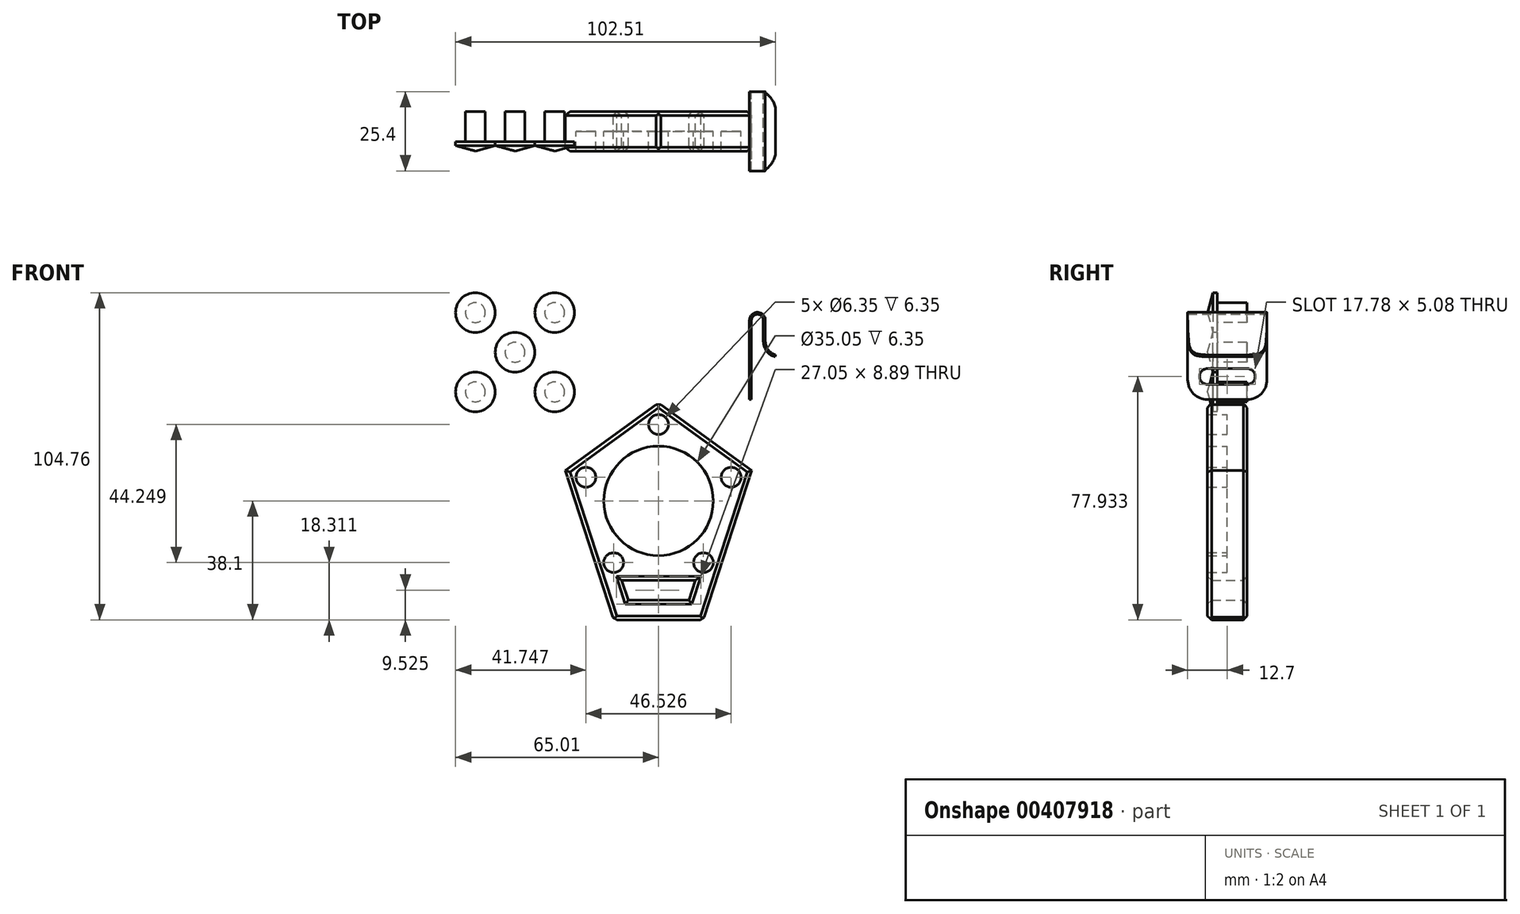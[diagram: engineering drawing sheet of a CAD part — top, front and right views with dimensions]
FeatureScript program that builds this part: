
annotation { "Feature Type Name" : "Feature", "Feature Type Description" : "" }
export const myFeature = defineFeature(function(context is Context, id is Id, definition is map)
    precondition{}
    {
        {
            var Q0;
            Q0=qCreatedBy(makeId("Front.planeOp"),FACE);
            var sketch = newSketch(context, id + "F0", { "sketchPlane" : qUnion([Q0])});
            skLineSegment(sketch, "E0.0", {"start": v(0, 31.4) * mm, "end": v(29.86, 9.7) * mm});
            skLineSegment(sketch, "E0.1", {"start": v(29.86, 9.7) * mm, "end": v(18.45, -25.4) * mm});
            skLineSegment(sketch, "E0.3", {"start": v(-18.45, -25.4) * mm, "end": v(-29.86, 9.7) * mm});
            skLineSegment(sketch, "E0.4", {"start": v(-29.86, 9.7) * mm, "end": v(0, 31.4) * mm});
            skLineSegment(sketch, "E1", {"start": v(-14.33, -38.1) * mm, "end": v(14.33, -38.1) * mm});
            skLineSegment(sketch, "E2", {"start": v(-9.71, -31.75) * mm, "end": v(9.71, -31.75) * mm});
            skLineSegment(sketch, "E3", {"start": v(11.78, -25.4) * mm, "end": v(-11.78, -25.4) * mm});
            skLineSegment(sketch, "E4", {"start": v(-18.45, -25.4) * mm, "end": v(-14.33, -38.1) * mm});
            skLineSegment(sketch, "E5", {"start": v(18.45, -25.4) * mm, "end": v(14.33, -38.1) * mm});
            skLineSegment(sketch, "E6", {"start": v(-11.78, -25.4) * mm, "end": v(-9.71, -31.75) * mm});
            skLineSegment(sketch, "E7", {"start": v(11.78, -25.4) * mm, "end": v(9.71, -31.75) * mm});
            skCircle(sketch, "E8", {"center": v(0, 0) * mm, "radius": 17.53 * mm});
            skLineSegment(sketch, "E9", {"start": v(-29.86, 9.7) * mm, "end": v(0, 0) * mm, "construction": true});
            skLineSegment(sketch, "E10", {"start": v(0, 31.4) * mm, "end": v(0, 0) * mm, "construction": true});
            skLineSegment(sketch, "E11", {"start": v(0, 0) * mm, "end": v(29.86, 9.7) * mm, "construction": true});
            skLineSegment(sketch, "E12", {"start": v(0, 0) * mm, "end": v(-18.45, -25.4) * mm, "construction": true});
            skLineSegment(sketch, "E13", {"start": v(0, 0) * mm, "end": v(18.45, -25.4) * mm, "construction": true});
            skCircle(sketch, "E14", {"center": v(-23.26, 7.56) * mm, "radius": 3.18 * mm});
            skCircle(sketch, "E15", {"center": v(0, 24.46) * mm, "radius": 3.18 * mm});
            skCircle(sketch, "E16", {"center": v(23.26, 7.56) * mm, "radius": 3.18 * mm});
            skCircle(sketch, "E17", {"center": v(14.38, -19.79) * mm, "radius": 3.18 * mm});
            skCircle(sketch, "E18", {"center": v(-14.38, -19.79) * mm, "radius": 3.18 * mm});
            skSolve(sketch);
        }
        {
            var Q0;
            Q0=makeQuery(id+"F0.imprint","IMPRINT",FACE,{"disambiguationData":[TD([[makeQuery(id+"F0.imprint","IMPRINT",EDGE,{"derivedFrom":sQuery(id+"F0.wireOp",EDGE,"E0.0")}),-1.0]])]});
            extrude(context, id + "F1", {"entities" : qUnion([Q0]), "endBound" : BoundingType.SYMMETRIC, "depth" : 12.7 * mm});
        }
        {
            var Q0;
            Q0=makeQuery(id+"F0.imprint","IMPRINT",FACE,{"disambiguationData":[TD([[makeQuery(id+"F0.imprint","IMPRINT",EDGE,{"derivedFrom":sQuery(id+"F0.wireOp",EDGE,"E8")}),1.0]])]});
            extrude(context, id + "F2", {"entities" : qUnion([Q0]), "operationType" : NewBodyOperationType.ADD, "oppositeDirection" : true, "depth" : 6.35 * mm});
        }
        {
            var Q0;
            Q0=makeQuery(id+"F0.imprint","IMPRINT",FACE,{"disambiguationData":[TD([[makeQuery(id+"F0.imprint","IMPRINT",EDGE,{"derivedFrom":sQuery(id+"F0.wireOp",EDGE,"E17")}),1.0]])]});
            var Q1;
            Q1=makeQuery(id+"F0.imprint","IMPRINT",FACE,{"disambiguationData":[TD([[makeQuery(id+"F0.imprint","IMPRINT",EDGE,{"derivedFrom":sQuery(id+"F0.wireOp",EDGE,"E16")}),1.0]])]});
            var Q2;
            Q2=makeQuery(id+"F0.imprint","IMPRINT",FACE,{"disambiguationData":[TD([[makeQuery(id+"F0.imprint","IMPRINT",EDGE,{"derivedFrom":sQuery(id+"F0.wireOp",EDGE,"E15")}),1.0]])]});
            var Q3;
            Q3=makeQuery(id+"F0.imprint","IMPRINT",FACE,{"disambiguationData":[TD([[makeQuery(id+"F0.imprint","IMPRINT",EDGE,{"derivedFrom":sQuery(id+"F0.wireOp",EDGE,"E14")}),1.0]])]});
            var Q4;
            Q4=makeQuery(id+"F0.imprint","IMPRINT",FACE,{"disambiguationData":[TD([[makeQuery(id+"F0.imprint","IMPRINT",EDGE,{"derivedFrom":sQuery(id+"F0.wireOp",EDGE,"E18")}),1.0]])]});
            extrude(context, id + "F3", {"entities" : qUnion([Q0, Q1, Q2, Q3, Q4]), "operationType" : NewBodyOperationType.ADD, "oppositeDirection" : true, "depth" : 6.35 * mm});
        }
        {
            var Q0;
            Q0=makeQuery(id+"F1.opExtrude","CAP_EDGE",EDGE,{"disambiguationData":[OSD([sQuery(id+"F0.wireOp",EDGE,"E2")])],"isStart":false});
            var Q1;
            Q1=makeQuery(id+"F1.opExtrude","CAP_EDGE",EDGE,{"disambiguationData":[OSD([sQuery(id+"F0.wireOp",EDGE,"E6")])],"isStart":false});
            var Q2;
            Q2=makeQuery(id+"F1.opExtrude","CAP_EDGE",EDGE,{"disambiguationData":[OSD([sQuery(id+"F0.wireOp",EDGE,"E3")])],"isStart":false});
            var Q3;
            Q3=makeQuery(id+"F1.opExtrude","CAP_EDGE",EDGE,{"disambiguationData":[OSD([sQuery(id+"F0.wireOp",EDGE,"E7")])],"isStart":false});
            var Q4;
            Q4=makeQuery(id+"F1.opExtrude","CAP_EDGE",EDGE,{"disambiguationData":[OSD([sQuery(id+"F0.wireOp",EDGE,"E2")])],"isStart":true});
            var Q5;
            Q5=makeQuery(id+"F1.opExtrude","CAP_EDGE",EDGE,{"disambiguationData":[OSD([sQuery(id+"F0.wireOp",EDGE,"E3")])],"isStart":true});
            var Q6;
            Q6=makeQuery(id+"F1.opExtrude","CAP_EDGE",EDGE,{"disambiguationData":[OSD([sQuery(id+"F0.wireOp",EDGE,"E6")])],"isStart":true});
            var Q7;
            Q7=makeQuery(id+"F1.opExtrude","CAP_EDGE",EDGE,{"disambiguationData":[OSD([sQuery(id+"F0.wireOp",EDGE,"E7")])],"isStart":true});
            var Q8;
            Q8=makeQuery(id+"F1.opExtrude","CAP_EDGE",EDGE,{"disambiguationData":[OSD([sQuery(id+"F0.wireOp",EDGE,"E1")])],"isStart":false});
            var Q9;
            Q9=makeQuery(id+"F1.opExtrude","CAP_EDGE",EDGE,{"disambiguationData":[OSD([sQuery(id+"F0.wireOp",EDGE,"E0.3"),sQuery(id+"F0.wireOp",EDGE,"E4")])],"isStart":false});
            var Q10;
            Q10=makeQuery(id+"F1.opExtrude","CAP_EDGE",EDGE,{"disambiguationData":[OSD([sQuery(id+"F0.wireOp",EDGE,"E0.0")])],"isStart":false});
            var Q11;
            Q11=makeQuery(id+"F1.opExtrude","CAP_EDGE",EDGE,{"disambiguationData":[OSD([sQuery(id+"F0.wireOp",EDGE,"E0.4")])],"isStart":false});
            var Q12;
            Q12=makeQuery(id+"F1.opExtrude","CAP_EDGE",EDGE,{"disambiguationData":[OSD([sQuery(id+"F0.wireOp",EDGE,"E0.4")])],"isStart":true});
            var Q13;
            Q13=makeQuery(id+"F1.opExtrude","CAP_EDGE",EDGE,{"disambiguationData":[OSD([sQuery(id+"F0.wireOp",EDGE,"E0.3"),sQuery(id+"F0.wireOp",EDGE,"E4")])],"isStart":true});
            var Q14;
            Q14=makeQuery(id+"F1.opExtrude","CAP_EDGE",EDGE,{"disambiguationData":[OSD([sQuery(id+"F0.wireOp",EDGE,"E0.1"),sQuery(id+"F0.wireOp",EDGE,"E5")])],"isStart":true});
            var Q15;
            Q15=makeQuery(id+"F1.opExtrude","CAP_EDGE",EDGE,{"disambiguationData":[OSD([sQuery(id+"F0.wireOp",EDGE,"E0.0")])],"isStart":true});
            var Q16;
            Q16=makeQuery(id+"F1.opExtrude","CAP_EDGE",EDGE,{"disambiguationData":[OSD([sQuery(id+"F0.wireOp",EDGE,"E1")])],"isStart":true});
            var Q17;
            Q17=makeQuery(id+"F1.opExtrude","CAP_EDGE",EDGE,{"disambiguationData":[OSD([sQuery(id+"F0.wireOp",EDGE,"E0.1"),sQuery(id+"F0.wireOp",EDGE,"E5")])],"isStart":false});
            chamfer(context, id + "F4", {"entities" : qUnion([Q0, Q1, Q2, Q3, Q4, Q5, Q6, Q7, Q8, Q9, Q10, Q11, Q12, Q13, Q14, Q15, Q16, Q17]), "width" : 1.27 * mm, "tangentPropagation" : true});
        }
        {
            var Q0;
            Q0=makeQuery(id+"F1.opExtrude","SWEPT_EDGE",EDGE,{"disambiguationData":[OSD([sQuery(id+"F0.wireOp",EDGE,"E0.0"),sQuery(id+"F0.wireOp",EDGE,"E0.4")])]});
            var Q1;
            Q1=makeQuery(id+"F1.opExtrude","SWEPT_EDGE",EDGE,{"disambiguationData":[OSD([sQuery(id+"F0.wireOp",EDGE,"E1"),sQuery(id+"F0.wireOp",EDGE,"E5")])]});
            var Q2;
            Q2=makeQuery(id+"F1.opExtrude","SWEPT_EDGE",EDGE,{"disambiguationData":[OSD([sQuery(id+"F0.wireOp",EDGE,"E1"),sQuery(id+"F0.wireOp",EDGE,"E4")])]});
            chamfer(context, id + "F5", {"entities" : qUnion([Q0, Q1, Q2]), "width" : 1.27 * mm, "tangentPropagation" : true});
        }
        {
            var Q0;
            Q0=qCreatedBy(makeId("Front.planeOp"),FACE);
            var sketch = newSketch(context, id + "F6", { "sketchPlane" : qUnion([Q0])});
            skLineSegment(sketch, "E19", {"start": v(-61.83, 38.2) * mm, "end": v(-61.83, 28.56) * mm});
            skLineSegment(sketch, "E20", {"start": v(-58.66, 28.56) * mm, "end": v(-61.83, 28.56) * mm});
            skLineSegment(sketch, "E21", {"start": v(-61.83, 38.2) * mm, "end": v(-65, 38.2) * mm});
            skLineSegment(sketch, "E22", {"start": v(-58.66, 41.26) * mm, "end": v(-58.66, 28.56) * mm});
            skLineSegment(sketch, "E23", {"start": v(-65, 38.2) * mm, "end": v(-65, 39.48) * mm});
            skLineSegment(sketch, "E24", {"start": v(-65, 39.48) * mm, "end": v(-58.66, 41.26) * mm});
            skLineSegment(sketch, "E25", {"start": v(-75.18, 34.9) * mm, "end": v(-45.79, 34.9) * mm, "construction": true});
            skSolve(sketch);
        }
        {
            var Q0;
            Q0 = qSketchRegion(id + "F6", true);
            var Q1;
            Q1=sQuery(id+"F6.wireOp",EDGE,"E22");
            revolve(context, id + "F7", {"entities" : qUnion([Q0]), "axis" : qUnion([Q1]), "revolveType" : RevolveType.FULL});
        }
        {
            var Q0;
            Q0=makeQuery(id+"F7.opRevolve","SWEPT_BODY",BODY,{"disambiguationData":[OSD([sQuery(id+"F6.wireOp",EDGE,"E19"),sQuery(id+"F6.wireOp",EDGE,"E20"),sQuery(id+"F6.wireOp",EDGE,"E21"),sQuery(id+"F6.wireOp",EDGE,"E22"),sQuery(id+"F6.wireOp",EDGE,"E23"),sQuery(id+"F6.wireOp",EDGE,"E24")])]});
            var Q1;
            Q1=sQuery(id+"F6.wireOp",EDGE,"E25");
            transform(context, id + "F8", {"entities" : qUnion([Q0]), "transformType" : TransformType.ROTATION, "transformAxis" : qUnion([Q1]), "angle" : 90 * degree, "makeCopy" : false});
        }
        {
            var Q0;
            Q0=makeQuery(id+"F7.opRevolve","SWEPT_BODY",BODY,{"disambiguationData":[OSD([sQuery(id+"F6.wireOp",EDGE,"E19"),sQuery(id+"F6.wireOp",EDGE,"E20"),sQuery(id+"F6.wireOp",EDGE,"E21"),sQuery(id+"F6.wireOp",EDGE,"E22"),sQuery(id+"F6.wireOp",EDGE,"E23"),sQuery(id+"F6.wireOp",EDGE,"E24")])]});
            transform(context, id + "F9", {"entities" : qUnion([Q0]), "transformType" : TransformType.TRANSLATION_3D, "dx" : 0 * mm, "dy" : 0 * mm, "dz" : 25.4 * mm, "makeCopy" : true});
        }
        {
            var Q0;
            Q0=makeQuery(id+"F9.opPattern","COPY",BODY,{"derivedFrom":makeQuery(id+"F7.opRevolve","SWEPT_BODY",BODY,{"disambiguationData":[OSD([sQuery(id+"F6.wireOp",EDGE,"E19"),sQuery(id+"F6.wireOp",EDGE,"E20"),sQuery(id+"F6.wireOp",EDGE,"E21"),sQuery(id+"F6.wireOp",EDGE,"E22"),sQuery(id+"F6.wireOp",EDGE,"E23"),sQuery(id+"F6.wireOp",EDGE,"E24")])]}),"instanceName":"1"});
            transform(context, id + "F10", {"entities" : qUnion([Q0]), "transformType" : TransformType.TRANSLATION_3D, "dx" : 25.4 * mm, "dy" : 0 * mm, "dz" : 0 * mm, "makeCopy" : true});
        }
        {
            var Q0;
            Q0=makeQuery(id+"F7.opRevolve","SWEPT_BODY",BODY,{"disambiguationData":[OSD([sQuery(id+"F6.wireOp",EDGE,"E19"),sQuery(id+"F6.wireOp",EDGE,"E20"),sQuery(id+"F6.wireOp",EDGE,"E21"),sQuery(id+"F6.wireOp",EDGE,"E22"),sQuery(id+"F6.wireOp",EDGE,"E23"),sQuery(id+"F6.wireOp",EDGE,"E24")])]});
            transform(context, id + "F11", {"entities" : qUnion([Q0]), "transformType" : TransformType.TRANSLATION_3D, "dx" : 25.4 * mm, "dy" : 0 * mm, "dz" : 0 * mm, "makeCopy" : true});
        }
        {
            var Q0;
            Q0=makeQuery(id+"F7.opRevolve","SWEPT_BODY",BODY,{"disambiguationData":[OSD([sQuery(id+"F6.wireOp",EDGE,"E19"),sQuery(id+"F6.wireOp",EDGE,"E20"),sQuery(id+"F6.wireOp",EDGE,"E21"),sQuery(id+"F6.wireOp",EDGE,"E22"),sQuery(id+"F6.wireOp",EDGE,"E23"),sQuery(id+"F6.wireOp",EDGE,"E24")])]});
            transform(context, id + "F12", {"entities" : qUnion([Q0]), "transformType" : TransformType.TRANSLATION_3D, "dx" : 12.7 * mm, "dy" : 0 * mm, "dz" : 12.7 * mm, "makeCopy" : true});
        }
        {
            var Q0;
            Q0=qCreatedBy(makeId("Front.planeOp"),FACE);
            var sketch = newSketch(context, id + "F13", { "sketchPlane" : qUnion([Q0])});
            skLineSegment(sketch, "E26", {"start": v(29.12, 57.83) * mm, "end": v(29.12, 32.43) * mm});
            skLineSegment(sketch, "E27", {"start": v(34.2, 57.83) * mm, "end": v(34.2, 51.1) * mm});
            skArc(sketch, "E28", {"start": v(29.12, 57.83) * mm, "mid": v(31.66, 60.37) * mm, "end": v(34.2, 57.83) * mm});
            skLineSegment(sketch, "E29", {"start": v(29.12, 57.83) * mm, "end": v(34.2, 57.83) * mm, "construction": true});
            skPoint(sketch, "E30.visualSharp", {"position": v(34.2, 47.67) * mm});
            skArc(sketch, "E30.filletArc", {"start": v(34.2, 51.1) * mm, "mid": v(35.12, 48.37) * mm, "end": v(37.5, 46.75) * mm});
            skLineSegment(sketch, "E31.0", {"start": v(29.76, 57.83) * mm, "end": v(29.76, 32.43) * mm});
            skArc(sketch, "E31.2", {"start": v(33.57, 51.1) * mm, "mid": v(34.62, 47.98) * mm, "end": v(37.33, 46.14) * mm});
            skLineSegment(sketch, "E31.3", {"start": v(33.57, 57.83) * mm, "end": v(33.57, 51.1) * mm});
            skArc(sketch, "E31.4", {"start": v(29.76, 57.83) * mm, "mid": v(31.66, 59.73) * mm, "end": v(33.57, 57.83) * mm});
            skPoint(sketch, "E32.visualSharp", {"position": v(37.6, 46.06) * mm});
            skPoint(sketch, "E33.visualSharp", {"position": v(36.65, 46.99) * mm});
            skLineSegment(sketch, "E34", {"start": v(37.33, 46.14) * mm, "end": v(37.5, 46.75) * mm});
            skLineSegment(sketch, "E35", {"start": v(29.12, 32.43) * mm, "end": v(29.76, 32.43) * mm});
            skSolve(sketch);
        }
        {
            var Q0;
            Q0=makeQuery(id+"F13.imprint","IMPRINT",FACE,{"disambiguationData":[TD([[makeQuery(id+"F13.imprint","IMPRINT",EDGE,{"derivedFrom":sQuery(id+"F13.wireOp",EDGE,"E26")}),1.0]])]});
            extrude(context, id + "F14", {"entities" : qUnion([Q0]), "endBound" : BoundingType.SYMMETRIC, "depth" : 25.4 * mm});
        }
        {
            var Q0;
            Q0=makeQuery(id+"F14.opExtrude","SWEPT_FACE",FACE,{"disambiguationData":[OSD([sQuery(id+"F13.wireOp",EDGE,"E26")])]});
            cPlane(context, id + "F15", {"entities" : qUnion([Q0]), "cplaneType" : CPlaneType.OFFSET, "offset" : 0 * mm, "oppositeDirection" : true, "width" : 152.4 * mm, "height" : 152.4 * mm});
        }
        {
            var Q0;
            Q0=qCreatedBy(id+"F15.planeOp",FACE);
            var sketch = newSketch(context, id + "F16", { "sketchPlane" : qUnion([Q0])});
            skLineSegment(sketch, "E36", {"start": v(0, 58.88) * mm, "end": v(25.4, 58.88) * mm, "construction": true});
            skLineSegment(sketch, "E37", {"start": v(25.4, 58.88) * mm, "end": v(25.4, 33.48) * mm, "construction": true});
            skLineSegment(sketch, "E38", {"start": v(25.4, 33.48) * mm, "end": v(0, 33.48) * mm, "construction": true});
            skLineSegment(sketch, "E39", {"start": v(0, 33.48) * mm, "end": v(0, 58.88) * mm, "construction": true});
            skLineSegment(sketch, "E40", {"start": v(0, 39.83) * mm, "end": v(0, 33.48) * mm, "construction": true});
            skLineSegment(sketch, "E41", {"start": v(0, 39.83) * mm, "end": v(6.35, 39.83) * mm});
            skLineSegment(sketch, "E42", {"start": v(6.35, 39.83) * mm, "end": v(0, 39.83) * mm});
            skLineSegment(sketch, "E43", {"start": v(0, 39.83) * mm, "end": v(-6.35, 39.83) * mm});
            skArc(sketch, "E44.0.startCap", {"start": v(6.35, 42.37) * mm, "mid": v(8.9, 39.83) * mm, "end": v(6.35, 37.3) * mm});
            skArc(sketch, "E44.0.endCap", {"start": v(0, 37.3) * mm, "mid": v(-2.54, 39.83) * mm, "end": v(0, 42.37) * mm});
            skLineSegment(sketch, "E44.0.left", {"start": v(6.35, 37.3) * mm, "end": v(0, 37.3) * mm});
            skLineSegment(sketch, "E44.0.right", {"start": v(6.35, 42.37) * mm, "end": v(0, 42.37) * mm});
            skArc(sketch, "E44.1.startCap", {"start": v(0, 42.37) * mm, "mid": v(2.54, 39.83) * mm, "end": v(0, 37.3) * mm});
            skArc(sketch, "E44.1.endCap", {"start": v(-6.35, 37.3) * mm, "mid": v(-8.9, 39.83) * mm, "end": v(-6.35, 42.37) * mm});
            skLineSegment(sketch, "E44.1.left", {"start": v(0, 37.3) * mm, "end": v(-6.35, 37.3) * mm});
            skLineSegment(sketch, "E44.1.right", {"start": v(0, 42.37) * mm, "end": v(-6.35, 42.37) * mm});
            skSolve(sketch);
        }
        {
            var Q0;
            Q0 = qSketchRegion(id + "F16", true);
            extrude(context, id + "F17", {"entities" : qUnion([Q0]), "operationType" : NewBodyOperationType.REMOVE, "oppositeDirection" : true, "depth" : 0.64 * mm});
        }
        {
            var Q0;
            Q0=makeQuery(id+"F14.opExtrude","CAP_EDGE",EDGE,{"disambiguationData":[OSD([sQuery(id+"F13.wireOp",EDGE,"E35")])],"isStart":false});
            var Q1;
            Q1=makeQuery(id+"F14.opExtrude","CAP_EDGE",EDGE,{"disambiguationData":[OSD([sQuery(id+"F13.wireOp",EDGE,"E34")])],"isStart":false});
            fillet(context, id + "F18", {"entities" : qUnion([Q0, Q1]), "radius" : 6.35 * mm, "tangentPropagation" : true, "allowEdgeOverflow" : false});
        }
        {
            var Q0;
            Q0=makeQuery(id+"F14.opExtrude","CAP_EDGE",EDGE,{"disambiguationData":[OSD([sQuery(id+"F13.wireOp",EDGE,"E34")])],"isStart":true});
            var Q1;
            Q1=makeQuery(id+"F14.opExtrude","CAP_EDGE",EDGE,{"disambiguationData":[OSD([sQuery(id+"F13.wireOp",EDGE,"E35")])],"isStart":true});
            fillet(context, id + "F19", {"entities" : qUnion([Q0, Q1]), "radius" : 6.35 * mm, "tangentPropagation" : true, "allowEdgeOverflow" : false});
        }
    });
